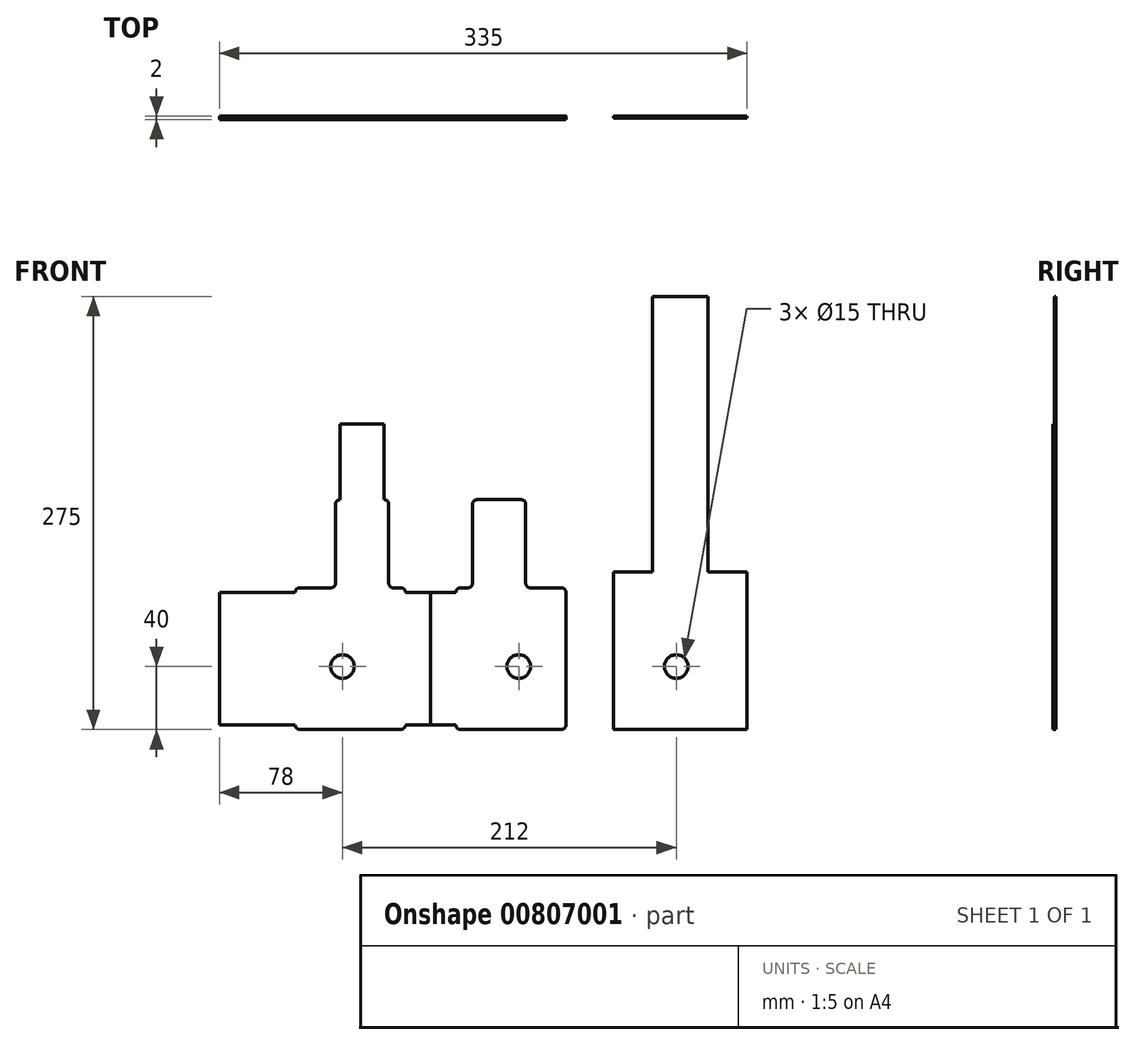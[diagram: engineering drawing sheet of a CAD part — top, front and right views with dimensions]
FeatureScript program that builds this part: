
annotation { "Feature Type Name" : "Feature", "Feature Type Description" : "" }
export const myFeature = defineFeature(function(context is Context, id is Id, definition is map)
    precondition{}
    {
        {
            var Q0;
            Q0=qCreatedBy(makeId("Front.planeOp"),FACE);
            var sketch = newSketch(context, id + "F0", { "sketchPlane" : qUnion([Q0])});
            skCircle(sketch, "E0", {"center": v(0, 0) * mm, "radius": 7.5 * mm});
            skLineSegment(sketch, "E1", {"start": v(20, 60) * mm, "end": v(20, 235) * mm});
            skLineSegment(sketch, "E2", {"start": v(20, 235) * mm, "end": v(-15, 235) * mm});
            skLineSegment(sketch, "E3", {"start": v(-15, 235) * mm, "end": v(-15, 60) * mm});
            skLineSegment(sketch, "E4", {"start": v(-15, 60) * mm, "end": v(-40, 60) * mm});
            skLineSegment(sketch, "E5", {"start": v(-40, 60) * mm, "end": v(-40, -40) * mm});
            skLineSegment(sketch, "E6", {"start": v(-40, -40) * mm, "end": v(45, -40) * mm});
            skLineSegment(sketch, "E7", {"start": v(45, -40) * mm, "end": v(45, 60) * mm});
            skLineSegment(sketch, "E8", {"start": v(45, 60) * mm, "end": v(20, 60) * mm});
            skSolve(sketch);
        }
        {
            var Q0;
            Q0=makeQuery(id+"F0.imprint","IMPRINT",FACE,{"disambiguationData":[TD([[makeQuery(id+"F0.imprint","IMPRINT",EDGE,{"derivedFrom":sQuery(id+"F0.wireOp",EDGE,"E0")}),-1.0]])]});
            extrude(context, id + "F1", {"entities" : qUnion([Q0]), "depth" : 1 * mm, "offsetDistance" : 25 * mm});
        }
        {
            var Q0;
            Q0=qCreatedBy(makeId("Front.planeOp"),FACE);
            var sketch = newSketch(context, id + "F2", { "sketchPlane" : qUnion([Q0])});
            skCircle(sketch, "E9", {"center": v(-100, 0) * mm, "radius": 7.5 * mm});
            skCircle(sketch, "E10", {"center": v(-100, 0) * mm, "radius": 110 * mm, "construction": true});
            skLineSegment(sketch, "E11.bottom", {"start": v(-103, 30) * mm, "end": v(-122, 30) * mm});
            skLineSegment(sketch, "E11.top", {"start": v(-103, 98) * mm, "end": v(-122, 98) * mm});
            skLineSegment(sketch, "E11.left", {"start": v(-103, 30) * mm, "end": v(-103, 98) * mm});
            skLineSegment(sketch, "E11.right", {"start": v(-122, 30) * mm, "end": v(-122, 98) * mm});
            skLineSegment(sketch, "E12.bottom", {"start": v(-95.6, 106) * mm, "end": v(-129.4, 106) * mm});
            skLineSegment(sketch, "E12.top", {"start": v(-95.6, 50) * mm, "end": v(-129.4, 50) * mm});
            skLineSegment(sketch, "E12.left", {"start": v(-95.6, 106) * mm, "end": v(-95.6, 50) * mm});
            skLineSegment(sketch, "E12.right", {"start": v(-129.4, 106) * mm, "end": v(-129.4, 50) * mm});
            skLineSegment(sketch, "E13.bottom", {"start": v(-70, 50) * mm, "end": v(-140, 50) * mm});
            skLineSegment(sketch, "E13.top", {"start": v(-70, -40) * mm, "end": v(-140, -40) * mm});
            skLineSegment(sketch, "E13.left", {"start": v(-70, 50) * mm, "end": v(-70, -40) * mm});
            skLineSegment(sketch, "E13.right", {"start": v(-140, 50) * mm, "end": v(-140, -40) * mm});
            skLineSegment(sketch, "E14", {"start": v(-112.5, 98) * mm, "end": v(-112.5, 106) * mm, "construction": true});
            skSolve(sketch);
        }
        {
            var Q0;
            Q0=makeQuery(id+"F2.imprint","IMPRINT",FACE,{"disambiguationData":[TD([[makeQuery(id+"F2.imprint","IMPRINT",EDGE,{"derivedFrom":sQuery(id+"F2.wireOp",EDGE,"E9")}),-1.0]])]});
            var Q1;
            {var subQ1=sQuery(id+"F2.wireOp",EDGE,"E11.top");Q1=makeQuery(id+"F2.imprint","IMPRINT",FACE,{"disambiguationData":[TD([[makeQuery(id+"F2.imprint","IMPRINT",EDGE,{"derivedFrom":subQ1}),-1.0]])]});}
            var Q2;
            {var subQ0=sQuery(id+"F2.wireOp",EDGE,"E11.top");Q2=makeQuery(id+"F2.imprint","IMPRINT",FACE,{"disambiguationData":[TD([[makeQuery(id+"F2.imprint","IMPRINT",EDGE,{"derivedFrom":subQ0}),1.0]])]});}
            var Q3;
            {var subQ0=sQuery(id+"F2.wireOp",EDGE,"E11.bottom");Q3=makeQuery(id+"F2.imprint","IMPRINT",FACE,{"disambiguationData":[TD([[makeQuery(id+"F2.imprint","IMPRINT",EDGE,{"derivedFrom":subQ0}),-1.0]])]});}
            extrude(context, id + "F3", {"entities" : qUnion([Q0, Q1, Q2, Q3]), "depth" : 2 * mm, "offsetDistance" : 25 * mm});
        }
        {
            var Q0;
            Q0=makeQuery(id+"F3.opExtrude","SWEPT_EDGE",EDGE,{"disambiguationData":[OSD([sQuery(id+"F2.wireOp",EDGE,"E12.right"),sQuery(id+"F2.wireOp",EDGE,"E13.bottom")])]});
            var Q1;
            Q1=makeQuery(id+"F3.opExtrude","SWEPT_EDGE",EDGE,{"disambiguationData":[OSD([sQuery(id+"F2.wireOp",EDGE,"E12.bottom"),sQuery(id+"F2.wireOp",EDGE,"E12.right")])]});
            var Q2;
            Q2=makeQuery(id+"F3.opExtrude","SWEPT_EDGE",EDGE,{"disambiguationData":[OSD([sQuery(id+"F2.wireOp",EDGE,"E12.bottom"),sQuery(id+"F2.wireOp",EDGE,"E12.left")])]});
            var Q3;
            Q3=makeQuery(id+"F3.opExtrude","SWEPT_EDGE",EDGE,{"disambiguationData":[OSD([sQuery(id+"F2.wireOp",EDGE,"E12.left"),sQuery(id+"F2.wireOp",EDGE,"E13.bottom")])]});
            var Q4;
            Q4=makeQuery(id+"F3.opExtrude","SWEPT_EDGE",EDGE,{"disambiguationData":[OSD([sQuery(id+"F2.wireOp",EDGE,"E13.bottom"),sQuery(id+"F2.wireOp",EDGE,"E13.left")])]});
            var Q5;
            Q5=makeQuery(id+"F3.opExtrude","SWEPT_EDGE",EDGE,{"disambiguationData":[OSD([sQuery(id+"F2.wireOp",EDGE,"E13.bottom"),sQuery(id+"F2.wireOp",EDGE,"E13.right")])]});
            var Q6;
            Q6=makeQuery(id+"F3.opExtrude","SWEPT_EDGE",EDGE,{"disambiguationData":[OSD([sQuery(id+"F2.wireOp",EDGE,"E13.top"),sQuery(id+"F2.wireOp",EDGE,"E13.right")])]});
            var Q7;
            Q7=makeQuery(id+"F3.opExtrude","SWEPT_EDGE",EDGE,{"disambiguationData":[OSD([sQuery(id+"F2.wireOp",EDGE,"E13.top"),sQuery(id+"F2.wireOp",EDGE,"E13.left")])]});
            fillet(context, id + "F4", {"entities" : qUnion([Q0, Q1, Q2, Q3, Q4, Q5, Q6, Q7]), "radius" : 3 * mm, "tangentPropagation" : true, "allowEdgeOverflow" : false});
        }
        {
            var Q0;
            Q0=makeQuery(id+"F3.opExtrude","SWEPT_FACE",FACE,{"disambiguationData":[OSD([sQuery(id+"F2.wireOp",EDGE,"E13.right")])]});
            var sketch = newSketch(context, id + "F5", { "sketchPlane" : qUnion([Q0])});
            skLineSegment(sketch, "E15.bottom", {"start": v(0, 47) * mm, "end": v(2, 47) * mm});
            skLineSegment(sketch, "E15.top", {"start": v(0, -37) * mm, "end": v(2, -37) * mm});
            skLineSegment(sketch, "E15.left", {"start": v(0, 47) * mm, "end": v(0, -37) * mm});
            skLineSegment(sketch, "E15.right", {"start": v(2, 47) * mm, "end": v(2, -37) * mm});
            skSolve(sketch);
        }
        {
            var Q0;
            Q0 = qSketchRegion(id + "F5", true);
            extrude(context, id + "F6", {"entities" : qUnion([Q0]), "operationType" : NewBodyOperationType.ADD, "depth" : 16 * mm, "offsetDistance" : 25 * mm});
        }
        {
            var Q0;
            Q0=makeQuery(id+"F3.opExtrude","SWEPT_BODY",BODY,{"disambiguationData":[OSD([sQuery(id+"F2.wireOp",EDGE,"E9"),sQuery(id+"F2.wireOp",EDGE,"E12.bottom"),sQuery(id+"F2.wireOp",EDGE,"E12.left"),sQuery(id+"F2.wireOp",EDGE,"E12.right"),sQuery(id+"F2.wireOp",EDGE,"E13.bottom"),sQuery(id+"F2.wireOp",EDGE,"E13.top"),sQuery(id+"F2.wireOp",EDGE,"E13.left"),sQuery(id+"F2.wireOp",EDGE,"E13.right")])]});
            var Q1;
            Q1=makeQuery(id+"F6.opExtrude","CAP_FACE",FACE,{"disambiguationData":[OSD([sQuery(id+"F5.wireOp",EDGE,"E15.bottom"),sQuery(id+"F5.wireOp",EDGE,"E15.top"),sQuery(id+"F5.wireOp",EDGE,"E15.left"),sQuery(id+"F5.wireOp",EDGE,"E15.right")])],"isStart":false});
            mirror(context, id + "F7", {"operationType" : NewBodyOperationType.ADD, "entities" : qUnion([Q0]), "mirrorPlane" : qUnion([Q1])});
        }
        {
            var Q0;
            Q0=makeQuery(id+"F7.opPattern","COPY",FACE,{"derivedFrom":makeQuery(id+"F3.opExtrude","SWEPT_FACE",FACE,{"disambiguationData":[OSD([sQuery(id+"F2.wireOp",EDGE,"E13.left")])]}),"instanceName":"1"});
            var sketch = newSketch(context, id + "F8", { "sketchPlane" : qUnion([Q0])});
            skLineSegment(sketch, "E16.bottom", {"start": v(0, 47) * mm, "end": v(2, 47) * mm});
            skLineSegment(sketch, "E16.top", {"start": v(0, -37) * mm, "end": v(2, -37) * mm});
            skLineSegment(sketch, "E16.left", {"start": v(0, 47) * mm, "end": v(0, -37) * mm});
            skLineSegment(sketch, "E16.right", {"start": v(2, 47) * mm, "end": v(2, -37) * mm});
            skSolve(sketch);
        }
        {
            var Q0;
            Q0 = qSketchRegion(id + "F8", true);
            extrude(context, id + "F9", {"entities" : qUnion([Q0]), "operationType" : NewBodyOperationType.ADD, "depth" : 48 * mm, "offsetDistance" : 25 * mm});
        }
        {
            var Q0;
            Q0=makeQuery(id+"F7.opPattern","COPY",FACE,{"derivedFrom":makeQuery(id+"F3.opExtrude","SWEPT_FACE",FACE,{"disambiguationData":[OSD([sQuery(id+"F2.wireOp",EDGE,"E12.bottom")])]}),"instanceName":"1"});
            var sketch = newSketch(context, id + "F10", { "sketchPlane" : qUnion([Q0])});
            skLineSegment(sketch, "E17.bottom", {"start": v(-185.6, 0) * mm, "end": v(-213.4, 0) * mm});
            skLineSegment(sketch, "E17.top", {"start": v(-185.6, -2) * mm, "end": v(-213.4, -2) * mm});
            skLineSegment(sketch, "E17.left", {"start": v(-185.6, 0) * mm, "end": v(-185.6, -2) * mm});
            skLineSegment(sketch, "E17.right", {"start": v(-213.4, 0) * mm, "end": v(-213.4, -2) * mm});
            skSolve(sketch);
        }
        {
            var Q0;
            Q0 = qSketchRegion(id + "F10", true);
            extrude(context, id + "F11", {"entities" : qUnion([Q0]), "operationType" : NewBodyOperationType.ADD, "depth" : 48 * mm, "offsetDistance" : 25 * mm});
        }
    });
